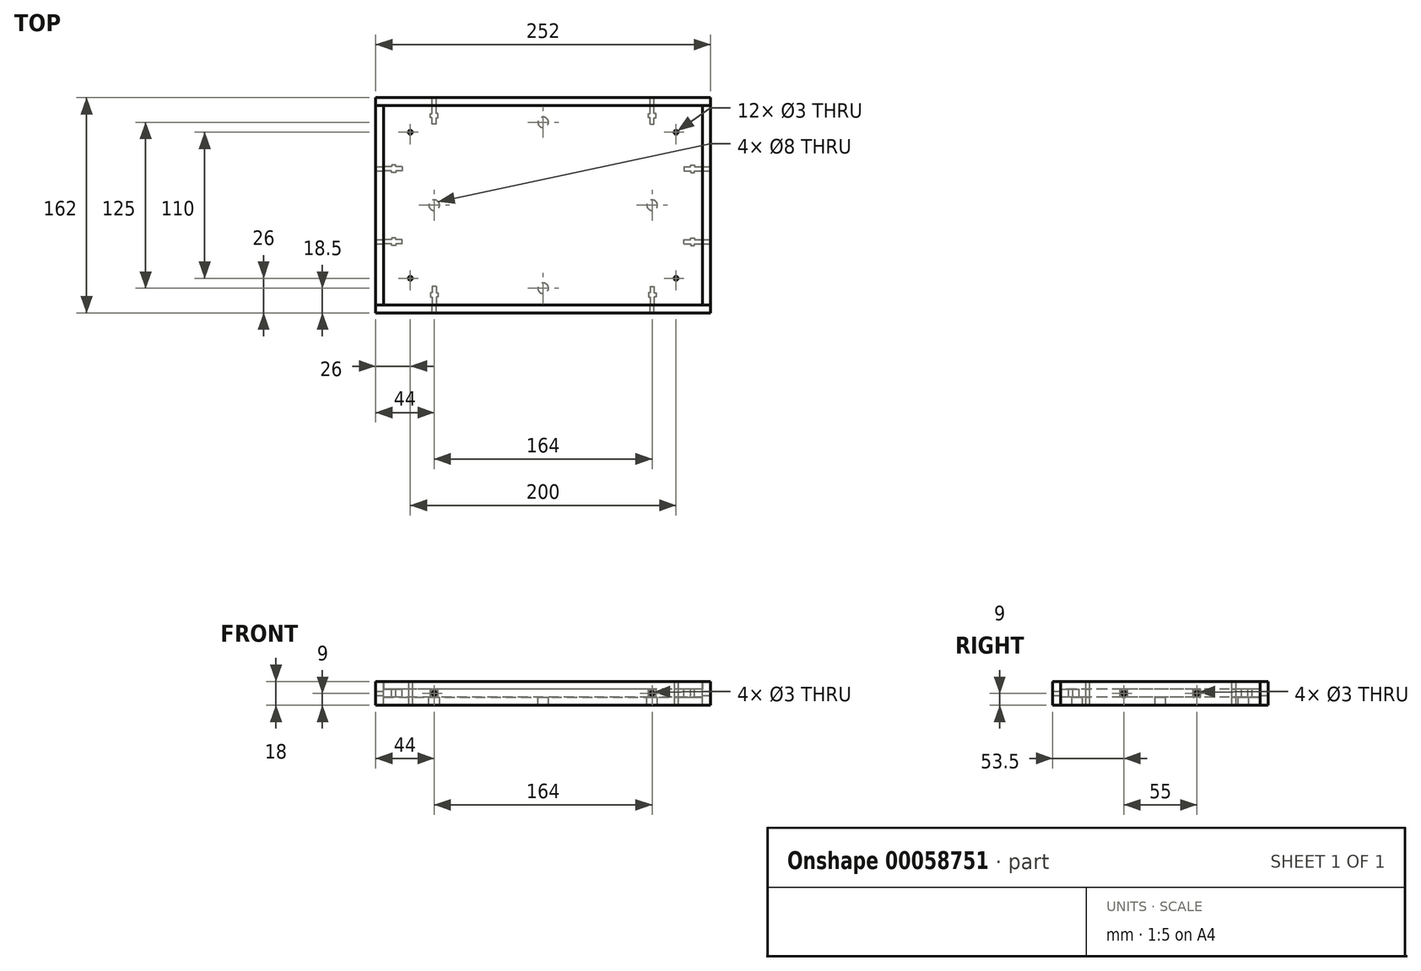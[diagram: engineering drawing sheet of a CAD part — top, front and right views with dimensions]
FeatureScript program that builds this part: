
annotation { "Feature Type Name" : "Feature", "Feature Type Description" : "" }
export const myFeature = defineFeature(function(context is Context, id is Id, definition is map)
    precondition{}
    {
        {
            var Q0;
            Q0=qCreatedBy(makeId("Top.planeOp"),FACE);
            var sketch = newSketch(context, id + "F25", { "sketchPlane" : qUnion([Q0])});
            skLineSegment(sketch, "E0.rect.bottom", {"start": v(120, 75) * mm, "end": v(-120, 75) * mm});
            skLineSegment(sketch, "E0.rect.top", {"start": v(120, -75) * mm, "end": v(-120, -75) * mm});
            skLineSegment(sketch, "E0.rect.left", {"start": v(120, 75) * mm, "end": v(120, -75) * mm});
            skLineSegment(sketch, "E0.rect.right", {"start": v(-120, 75) * mm, "end": v(-120, -75) * mm});
            skPoint(sketch, "E0.rect.middle", {"position": v(0, 0) * mm});
            skSolve(sketch);
        }
        {
            var Q0;
            Q0=makeQuery(id+"F25.imprint","IMPRINT",FACE,{"disambiguationData":[TD([[makeQuery(id+"F25.imprint","IMPRINT",EDGE,{"derivedFrom":sQuery(id+"F25.wireOp",EDGE,"E0.rect.bottom")}),1.0]])]});
            extrude(context, id + "F0", {"entities" : qUnion([Q0]), "depth" : 6 * mm});
        }
        {
            var Q0;
            Q0=makeQuery(id+"F0.opExtrude","CAP_FACE",FACE,{"disambiguationData":[OSD([sQuery(id+"F25.wireOp",EDGE,"E0.rect.bottom"),sQuery(id+"F25.wireOp",EDGE,"E0.rect.top"),sQuery(id+"F25.wireOp",EDGE,"E0.rect.left"),sQuery(id+"F25.wireOp",EDGE,"E0.rect.right")])],"isStart":true});
            extrude(context, id + "F1", {"entities" : qUnion([Q0]), "depth" : 6 * mm});
        }
        {
            var Q0;
            Q0=makeQuery(id+"F1.opExtrude","CAP_FACE",FACE,{"disambiguationData":[OSD([sQuery(id+"F25.wireOp",EDGE,"E0.rect.bottom"),sQuery(id+"F25.wireOp",EDGE,"E0.rect.top"),sQuery(id+"F25.wireOp",EDGE,"E0.rect.left"),sQuery(id+"F25.wireOp",EDGE,"E0.rect.right")])],"isStart":true});
            var sketch = newSketch(context, id + "F2", { "sketchPlane" : qUnion([Q0])});
            skLineSegment(sketch, "E1", {"start": v(106, -27.5) * mm, "end": v(120, -27.5) * mm, "construction": true});
            skLineSegment(sketch, "E2", {"start": v(120, -29) * mm, "end": v(114, -29) * mm});
            skLineSegment(sketch, "E3", {"start": v(114, -29) * mm, "end": v(114, -30.35) * mm});
            skLineSegment(sketch, "E4", {"start": v(114, -30.35) * mm, "end": v(111, -30.35) * mm});
            skLineSegment(sketch, "E5", {"start": v(111, -30.35) * mm, "end": v(111, -29) * mm});
            skLineSegment(sketch, "E6", {"start": v(111, -29) * mm, "end": v(106, -29) * mm});
            skLineSegment(sketch, "E7", {"start": v(106, -29) * mm, "end": v(106, -27.5) * mm});
            skLineSegment(sketch, "E8", {"start": v(120, -29) * mm, "end": v(120, -27.5) * mm});
            skLineSegment(sketch, "E9.MirrorCS", {"start": v(120, -26) * mm, "end": v(120, -27.5) * mm});
            skLineSegment(sketch, "E10.MirrorCS", {"start": v(120, -26) * mm, "end": v(114, -26) * mm});
            skLineSegment(sketch, "E11.MirrorCS", {"start": v(114, -26) * mm, "end": v(114, -24.65) * mm});
            skLineSegment(sketch, "E12.MirrorCS", {"start": v(114, -24.65) * mm, "end": v(111, -24.65) * mm});
            skLineSegment(sketch, "E13.MirrorCS", {"start": v(111, -24.65) * mm, "end": v(111, -26) * mm});
            skLineSegment(sketch, "E14.MirrorCS", {"start": v(111, -26) * mm, "end": v(106, -26) * mm});
            skLineSegment(sketch, "E15.MirrorCS", {"start": v(106, -26) * mm, "end": v(106, -27.5) * mm});
            skLineSegment(sketch, "E16", {"start": v(82, -61) * mm, "end": v(82, -75) * mm, "construction": true});
            skLineSegment(sketch, "E17", {"start": v(82, -75) * mm, "end": v(80.5, -75) * mm});
            skLineSegment(sketch, "E18", {"start": v(80.5, -75) * mm, "end": v(80.5, -69) * mm});
            skLineSegment(sketch, "E19", {"start": v(80.5, -69) * mm, "end": v(79.15, -69) * mm});
            skLineSegment(sketch, "E20", {"start": v(79.15, -69) * mm, "end": v(79.15, -66) * mm});
            skLineSegment(sketch, "E21", {"start": v(79.15, -66) * mm, "end": v(80.5, -66) * mm});
            skLineSegment(sketch, "E22", {"start": v(80.5, -66) * mm, "end": v(80.5, -61) * mm});
            skLineSegment(sketch, "E23", {"start": v(80.5, -61) * mm, "end": v(82, -61) * mm});
            skLineSegment(sketch, "E24.MirrorCS", {"start": v(82, -75) * mm, "end": v(83.5, -75) * mm});
            skLineSegment(sketch, "E25.MirrorCS", {"start": v(83.5, -75) * mm, "end": v(83.5, -69) * mm});
            skLineSegment(sketch, "E26.MirrorCS", {"start": v(83.5, -69) * mm, "end": v(84.85, -69) * mm});
            skLineSegment(sketch, "E27.MirrorCS", {"start": v(84.85, -69) * mm, "end": v(84.85, -66) * mm});
            skLineSegment(sketch, "E28.MirrorCS", {"start": v(84.85, -66) * mm, "end": v(83.5, -66) * mm});
            skLineSegment(sketch, "E29.MirrorCS", {"start": v(83.5, -66) * mm, "end": v(83.5, -61) * mm});
            skLineSegment(sketch, "E30.MirrorCS", {"start": v(83.5, -61) * mm, "end": v(82, -61) * mm});
            skSolve(sketch);
        }
        {
            var Q0;
            Q0=makeQuery(id+"F2.imprint","IMPRINT",FACE,{"disambiguationData":[TD([[makeQuery(id+"F2.imprint","IMPRINT",EDGE,{"derivedFrom":sQuery(id+"F2.wireOp",EDGE,"E17")}),-1.0]])]});
            var Q1;
            Q1=makeQuery(id+"F2.imprint","IMPRINT",FACE,{"disambiguationData":[TD([[makeQuery(id+"F2.imprint","IMPRINT",EDGE,{"derivedFrom":sQuery(id+"F2.wireOp",EDGE,"E2")}),-1.0]])]});
            var Q2;
            Q2=makeQuery(id+"F1.opExtrude","CAP_FACE",FACE,{"disambiguationData":[OSD([sQuery(id+"F25.wireOp",EDGE,"E0.rect.bottom"),sQuery(id+"F25.wireOp",EDGE,"E0.rect.top"),sQuery(id+"F25.wireOp",EDGE,"E0.rect.left"),sQuery(id+"F25.wireOp",EDGE,"E0.rect.right")])],"isStart":false});
            extrude(context, id + "F3", {"entities" : qUnion([Q0, Q1]), "endBound" : BoundingType.UP_TO_SURFACE, "oppositeDirection" : true, "endBoundEntityFace" : qUnion([Q2]), "depth" : 25 * mm});
        }
        {
            var Q0;
            Q0=makeQuery(id+"F3.opExtrude","SWEPT_BODY",BODY,{"disambiguationData":[OSD([sQuery(id+"F2.wireOp",EDGE,"E17"),sQuery(id+"F2.wireOp",EDGE,"E18"),sQuery(id+"F2.wireOp",EDGE,"E19"),sQuery(id+"F2.wireOp",EDGE,"E20"),sQuery(id+"F2.wireOp",EDGE,"E21"),sQuery(id+"F2.wireOp",EDGE,"E22"),sQuery(id+"F2.wireOp",EDGE,"E23"),sQuery(id+"F2.wireOp",EDGE,"E24.MirrorCS"),sQuery(id+"F2.wireOp",EDGE,"E25.MirrorCS"),sQuery(id+"F2.wireOp",EDGE,"E26.MirrorCS"),sQuery(id+"F2.wireOp",EDGE,"E27.MirrorCS"),sQuery(id+"F2.wireOp",EDGE,"E28.MirrorCS"),sQuery(id+"F2.wireOp",EDGE,"E29.MirrorCS"),sQuery(id+"F2.wireOp",EDGE,"E30.MirrorCS")])]});
            var Q1;
            Q1=makeQuery(id+"F3.opExtrude","SWEPT_BODY",BODY,{"disambiguationData":[OSD([sQuery(id+"F2.wireOp",EDGE,"E2"),sQuery(id+"F2.wireOp",EDGE,"E3"),sQuery(id+"F2.wireOp",EDGE,"E4"),sQuery(id+"F2.wireOp",EDGE,"E5"),sQuery(id+"F2.wireOp",EDGE,"E6"),sQuery(id+"F2.wireOp",EDGE,"E7"),sQuery(id+"F2.wireOp",EDGE,"E8"),sQuery(id+"F2.wireOp",EDGE,"E9.MirrorCS"),sQuery(id+"F2.wireOp",EDGE,"E10.MirrorCS"),sQuery(id+"F2.wireOp",EDGE,"E11.MirrorCS"),sQuery(id+"F2.wireOp",EDGE,"E12.MirrorCS"),sQuery(id+"F2.wireOp",EDGE,"E13.MirrorCS"),sQuery(id+"F2.wireOp",EDGE,"E14.MirrorCS"),sQuery(id+"F2.wireOp",EDGE,"E15.MirrorCS")])]});
            var Q2;
            Q2=qCreatedBy(makeId("Front.planeOp"),FACE);
            mirror(context, id + "F4", {"entities" : qUnion([Q0, Q1]), "mirrorPlane" : qUnion([Q2])});
        }
        {
            var Q0;
            Q0=makeQuery(id+"F3.opExtrude","SWEPT_BODY",BODY,{"disambiguationData":[OSD([sQuery(id+"F2.wireOp",EDGE,"E17"),sQuery(id+"F2.wireOp",EDGE,"E18"),sQuery(id+"F2.wireOp",EDGE,"E19"),sQuery(id+"F2.wireOp",EDGE,"E20"),sQuery(id+"F2.wireOp",EDGE,"E21"),sQuery(id+"F2.wireOp",EDGE,"E22"),sQuery(id+"F2.wireOp",EDGE,"E23"),sQuery(id+"F2.wireOp",EDGE,"E24.MirrorCS"),sQuery(id+"F2.wireOp",EDGE,"E25.MirrorCS"),sQuery(id+"F2.wireOp",EDGE,"E26.MirrorCS"),sQuery(id+"F2.wireOp",EDGE,"E27.MirrorCS"),sQuery(id+"F2.wireOp",EDGE,"E28.MirrorCS"),sQuery(id+"F2.wireOp",EDGE,"E29.MirrorCS"),sQuery(id+"F2.wireOp",EDGE,"E30.MirrorCS")])]});
            var Q1;
            Q1=makeQuery(id+"F3.opExtrude","SWEPT_BODY",BODY,{"disambiguationData":[OSD([sQuery(id+"F2.wireOp",EDGE,"E2"),sQuery(id+"F2.wireOp",EDGE,"E3"),sQuery(id+"F2.wireOp",EDGE,"E4"),sQuery(id+"F2.wireOp",EDGE,"E5"),sQuery(id+"F2.wireOp",EDGE,"E6"),sQuery(id+"F2.wireOp",EDGE,"E7"),sQuery(id+"F2.wireOp",EDGE,"E8"),sQuery(id+"F2.wireOp",EDGE,"E9.MirrorCS"),sQuery(id+"F2.wireOp",EDGE,"E10.MirrorCS"),sQuery(id+"F2.wireOp",EDGE,"E11.MirrorCS"),sQuery(id+"F2.wireOp",EDGE,"E12.MirrorCS"),sQuery(id+"F2.wireOp",EDGE,"E13.MirrorCS"),sQuery(id+"F2.wireOp",EDGE,"E14.MirrorCS"),sQuery(id+"F2.wireOp",EDGE,"E15.MirrorCS")])]});
            var Q2;
            Q2=makeQuery(id+"F4.opPattern","COPY",BODY,{"derivedFrom":makeQuery(id+"F3.opExtrude","SWEPT_BODY",BODY,{"disambiguationData":[OSD([sQuery(id+"F2.wireOp",EDGE,"E2"),sQuery(id+"F2.wireOp",EDGE,"E3"),sQuery(id+"F2.wireOp",EDGE,"E4"),sQuery(id+"F2.wireOp",EDGE,"E5"),sQuery(id+"F2.wireOp",EDGE,"E6"),sQuery(id+"F2.wireOp",EDGE,"E7"),sQuery(id+"F2.wireOp",EDGE,"E8"),sQuery(id+"F2.wireOp",EDGE,"E9.MirrorCS"),sQuery(id+"F2.wireOp",EDGE,"E10.MirrorCS"),sQuery(id+"F2.wireOp",EDGE,"E11.MirrorCS"),sQuery(id+"F2.wireOp",EDGE,"E12.MirrorCS"),sQuery(id+"F2.wireOp",EDGE,"E13.MirrorCS"),sQuery(id+"F2.wireOp",EDGE,"E14.MirrorCS"),sQuery(id+"F2.wireOp",EDGE,"E15.MirrorCS")])]}),"instanceName":"1"});
            var Q3;
            Q3=makeQuery(id+"F4.opPattern","COPY",BODY,{"derivedFrom":makeQuery(id+"F3.opExtrude","SWEPT_BODY",BODY,{"disambiguationData":[OSD([sQuery(id+"F2.wireOp",EDGE,"E17"),sQuery(id+"F2.wireOp",EDGE,"E18"),sQuery(id+"F2.wireOp",EDGE,"E19"),sQuery(id+"F2.wireOp",EDGE,"E20"),sQuery(id+"F2.wireOp",EDGE,"E21"),sQuery(id+"F2.wireOp",EDGE,"E22"),sQuery(id+"F2.wireOp",EDGE,"E23"),sQuery(id+"F2.wireOp",EDGE,"E24.MirrorCS"),sQuery(id+"F2.wireOp",EDGE,"E25.MirrorCS"),sQuery(id+"F2.wireOp",EDGE,"E26.MirrorCS"),sQuery(id+"F2.wireOp",EDGE,"E27.MirrorCS"),sQuery(id+"F2.wireOp",EDGE,"E28.MirrorCS"),sQuery(id+"F2.wireOp",EDGE,"E29.MirrorCS"),sQuery(id+"F2.wireOp",EDGE,"E30.MirrorCS")])]}),"instanceName":"1"});
            var Q4;
            Q4=qCreatedBy(makeId("Right.planeOp"),FACE);
            mirror(context, id + "F5", {"operationType" : NewBodyOperationType.REMOVE, "entities" : qUnion([Q0, Q1, Q2, Q3]), "mirrorPlane" : qUnion([Q4])});
        }
        {
            var Q0;
            Q0=makeQuery(id+"F3.opExtrude","SWEPT_BODY",BODY,{"disambiguationData":[OSD([sQuery(id+"F2.wireOp",EDGE,"E17"),sQuery(id+"F2.wireOp",EDGE,"E18"),sQuery(id+"F2.wireOp",EDGE,"E19"),sQuery(id+"F2.wireOp",EDGE,"E20"),sQuery(id+"F2.wireOp",EDGE,"E21"),sQuery(id+"F2.wireOp",EDGE,"E22"),sQuery(id+"F2.wireOp",EDGE,"E23"),sQuery(id+"F2.wireOp",EDGE,"E24.MirrorCS"),sQuery(id+"F2.wireOp",EDGE,"E25.MirrorCS"),sQuery(id+"F2.wireOp",EDGE,"E26.MirrorCS"),sQuery(id+"F2.wireOp",EDGE,"E27.MirrorCS"),sQuery(id+"F2.wireOp",EDGE,"E28.MirrorCS"),sQuery(id+"F2.wireOp",EDGE,"E29.MirrorCS"),sQuery(id+"F2.wireOp",EDGE,"E30.MirrorCS")])]});
            var Q1;
            Q1=makeQuery(id+"F3.opExtrude","SWEPT_BODY",BODY,{"disambiguationData":[OSD([sQuery(id+"F2.wireOp",EDGE,"E2"),sQuery(id+"F2.wireOp",EDGE,"E3"),sQuery(id+"F2.wireOp",EDGE,"E4"),sQuery(id+"F2.wireOp",EDGE,"E5"),sQuery(id+"F2.wireOp",EDGE,"E6"),sQuery(id+"F2.wireOp",EDGE,"E7"),sQuery(id+"F2.wireOp",EDGE,"E8"),sQuery(id+"F2.wireOp",EDGE,"E9.MirrorCS"),sQuery(id+"F2.wireOp",EDGE,"E10.MirrorCS"),sQuery(id+"F2.wireOp",EDGE,"E11.MirrorCS"),sQuery(id+"F2.wireOp",EDGE,"E12.MirrorCS"),sQuery(id+"F2.wireOp",EDGE,"E13.MirrorCS"),sQuery(id+"F2.wireOp",EDGE,"E14.MirrorCS"),sQuery(id+"F2.wireOp",EDGE,"E15.MirrorCS")])]});
            var Q2;
            Q2=makeQuery(id+"F4.opPattern","COPY",BODY,{"derivedFrom":makeQuery(id+"F3.opExtrude","SWEPT_BODY",BODY,{"disambiguationData":[OSD([sQuery(id+"F2.wireOp",EDGE,"E2"),sQuery(id+"F2.wireOp",EDGE,"E3"),sQuery(id+"F2.wireOp",EDGE,"E4"),sQuery(id+"F2.wireOp",EDGE,"E5"),sQuery(id+"F2.wireOp",EDGE,"E6"),sQuery(id+"F2.wireOp",EDGE,"E7"),sQuery(id+"F2.wireOp",EDGE,"E8"),sQuery(id+"F2.wireOp",EDGE,"E9.MirrorCS"),sQuery(id+"F2.wireOp",EDGE,"E10.MirrorCS"),sQuery(id+"F2.wireOp",EDGE,"E11.MirrorCS"),sQuery(id+"F2.wireOp",EDGE,"E12.MirrorCS"),sQuery(id+"F2.wireOp",EDGE,"E13.MirrorCS"),sQuery(id+"F2.wireOp",EDGE,"E14.MirrorCS"),sQuery(id+"F2.wireOp",EDGE,"E15.MirrorCS")])]}),"instanceName":"1"});
            var Q3;
            Q3=makeQuery(id+"F4.opPattern","COPY",BODY,{"derivedFrom":makeQuery(id+"F3.opExtrude","SWEPT_BODY",BODY,{"disambiguationData":[OSD([sQuery(id+"F2.wireOp",EDGE,"E17"),sQuery(id+"F2.wireOp",EDGE,"E18"),sQuery(id+"F2.wireOp",EDGE,"E19"),sQuery(id+"F2.wireOp",EDGE,"E20"),sQuery(id+"F2.wireOp",EDGE,"E21"),sQuery(id+"F2.wireOp",EDGE,"E22"),sQuery(id+"F2.wireOp",EDGE,"E23"),sQuery(id+"F2.wireOp",EDGE,"E24.MirrorCS"),sQuery(id+"F2.wireOp",EDGE,"E25.MirrorCS"),sQuery(id+"F2.wireOp",EDGE,"E26.MirrorCS"),sQuery(id+"F2.wireOp",EDGE,"E27.MirrorCS"),sQuery(id+"F2.wireOp",EDGE,"E28.MirrorCS"),sQuery(id+"F2.wireOp",EDGE,"E29.MirrorCS"),sQuery(id+"F2.wireOp",EDGE,"E30.MirrorCS")])]}),"instanceName":"1"});
            var Q4;
            Q4=makeQuery(id+"F1.opExtrude","SWEPT_BODY",BODY,{"disambiguationData":[OSD([sQuery(id+"F25.wireOp",EDGE,"E0.rect.bottom"),sQuery(id+"F25.wireOp",EDGE,"E0.rect.top"),sQuery(id+"F25.wireOp",EDGE,"E0.rect.left"),sQuery(id+"F25.wireOp",EDGE,"E0.rect.right")])]});
            booleanBodies(context, id + "F6", {"operationType" : BooleanOperationType.SUBTRACTION, "tools" : qUnion([Q0, Q1, Q2, Q3]), "targets" : qUnion([Q4])});
        }
        {
            var Q0;
            Q0=makeQuery(id+"F1.opExtrude","CAP_FACE",FACE,{"disambiguationData":[OSD([sQuery(id+"F25.wireOp",EDGE,"E0.rect.bottom"),sQuery(id+"F25.wireOp",EDGE,"E0.rect.top"),sQuery(id+"F25.wireOp",EDGE,"E0.rect.left"),sQuery(id+"F25.wireOp",EDGE,"E0.rect.right")])],"isStart":false});
            var sketch = newSketch(context, id + "F7", { "sketchPlane" : qUnion([Q0])});
            skLineSegment(sketch, "E31", {"start": v(120, -75) * mm, "end": v(120, 75) * mm});
            skLineSegment(sketch, "E32", {"start": v(120, 75) * mm, "end": v(-120, 75) * mm});
            skLineSegment(sketch, "E33", {"start": v(-120, 75) * mm, "end": v(-120, -75) * mm});
            skLineSegment(sketch, "E34", {"start": v(-120, -75) * mm, "end": v(120, -75) * mm});
            skSolve(sketch);
        }
        {
            var Q0;
            Q0=qSketchRegion(id+"F7",true);
            extrude(context, id + "F8", {"entities" : qUnion([Q0]), "depth" : 6 * mm});
        }
        {
            var Q0;
            Q0=makeQuery(id+"F0.opExtrude","CAP_FACE",FACE,{"disambiguationData":[OSD([sQuery(id+"F25.wireOp",EDGE,"E0.rect.bottom"),sQuery(id+"F25.wireOp",EDGE,"E0.rect.top"),sQuery(id+"F25.wireOp",EDGE,"E0.rect.left"),sQuery(id+"F25.wireOp",EDGE,"E0.rect.right")])],"isStart":false});
            var sketch = newSketch(context, id + "F9", { "sketchPlane" : qUnion([Q0])});
            skPoint(sketch, "E35", {"position": v(82, 0) * mm});
            skPoint(sketch, "E36", {"position": v(0, -62.5) * mm});
            skPoint(sketch, "E37.MirrorP", {"position": v(0, 62.5) * mm});
            skPoint(sketch, "E38.MirrorP", {"position": v(-82, 0) * mm});
            skLineSegment(sketch, "E39", {"start": v(0, -62.5) * mm, "end": v(0, -75) * mm, "construction": true});
            skLineSegment(sketch, "E40", {"start": v(120, 0) * mm, "end": v(82, 0) * mm, "construction": true});
            skSolve(sketch);
        }
        {
            var Q0;
            Q0=sQuery(id+"F9.wireOp",VERTEX,"E35");
            var Q1;
            Q1=sQuery(id+"F9.wireOp",VERTEX,"E36");
            var Q2;
            Q2=sQuery(id+"F9.wireOp",VERTEX,"E37.MirrorP");
            var Q3;
            Q3=sQuery(id+"F9.wireOp",VERTEX,"E38.MirrorP");
            var Q4;
            Q4=makeQuery(id+"F8.opExtrude","SWEPT_BODY",BODY,{"disambiguationData":[OSD([sQuery(id+"F7.wireOp",EDGE,"E31"),sQuery(id+"F7.wireOp",EDGE,"E32"),sQuery(id+"F7.wireOp",EDGE,"E33"),sQuery(id+"F7.wireOp",EDGE,"E34")])]});
            hole(context, id + "F10", {"style" : HoleStyle.SIMPLE, "holeDiameter" : 8 * mm, "endStyle" : HoleEndStyle.THROUGH, "locations" : qUnion([Q0, Q1, Q2, Q3]), "scope" : qUnion([Q4])});
        }
        {
            var Q0;
            Q0=makeQuery(id+"F0.opExtrude","SWEPT_FACE",FACE,{"disambiguationData":[OSD([sQuery(id+"F25.wireOp",EDGE,"E0.rect.bottom")])]});
            var sketch = newSketch(context, id + "F11", { "sketchPlane" : qUnion([Q0])});
            skLineSegment(sketch, "E41", {"start": v(-126, 6) * mm, "end": v(-126, -12) * mm});
            skLineSegment(sketch, "E42", {"start": v(-126, -12) * mm, "end": v(126, -12) * mm});
            skLineSegment(sketch, "E43", {"start": v(126, -12) * mm, "end": v(126, 6) * mm});
            skLineSegment(sketch, "E44", {"start": v(126, 6) * mm, "end": v(-126, 6) * mm});
            skSolve(sketch);
        }
        {
            var Q0;
            Q0=qSketchRegion(id+"F11",true);
            extrude(context, id + "F12", {"entities" : qUnion([Q0]), "depth" : 6 * mm});
        }
        {
            var Q0;
            Q0=makeQuery(id+"F12.opExtrude","CAP_FACE",FACE,{"disambiguationData":[OSD([sQuery(id+"F11.wireOp",EDGE,"E41"),sQuery(id+"F11.wireOp",EDGE,"E42"),sQuery(id+"F11.wireOp",EDGE,"E43"),sQuery(id+"F11.wireOp",EDGE,"E44")])],"isStart":false});
            var sketch = newSketch(context, id + "F13", { "sketchPlane" : qUnion([Q0])});
            skLineSegment(sketch, "E45.0", {"start": v(-83.5, -6) * mm, "end": v(-83.5, 0) * mm, "construction": true});
            skLineSegment(sketch, "E46.0", {"start": v(-80.5, -6) * mm, "end": v(-80.5, 0) * mm, "construction": true});
            skLineSegment(sketch, "E47.0", {"start": v(80.5, -6) * mm, "end": v(80.5, 0) * mm, "construction": true});
            skLineSegment(sketch, "E48.0", {"start": v(83.5, -6) * mm, "end": v(83.5, 0) * mm, "construction": true});
            skLineSegment(sketch, "E49", {"start": v(-83.5, -3) * mm, "end": v(-80.5, -3) * mm, "construction": true});
            skLineSegment(sketch, "E50", {"start": v(80.5, -3) * mm, "end": v(83.5, -3) * mm, "construction": true});
            skPoint(sketch, "E51", {"position": v(-82, -3) * mm});
            skPoint(sketch, "E52", {"position": v(82, -3) * mm});
            skSolve(sketch);
        }
        {
            var Q0;
            Q0=sQuery(id+"F13.wireOp",VERTEX,"E51");
            var Q1;
            Q1=sQuery(id+"F13.wireOp",VERTEX,"E52");
            var Q2;
            Q2=makeQuery(id+"F12.opExtrude","SWEPT_BODY",BODY,{"disambiguationData":[OSD([sQuery(id+"F11.wireOp",EDGE,"E41"),sQuery(id+"F11.wireOp",EDGE,"E42"),sQuery(id+"F11.wireOp",EDGE,"E43"),sQuery(id+"F11.wireOp",EDGE,"E44")])]});
            hole(context, id + "F14", {"style" : HoleStyle.SIMPLE, "holeDiameter" : 3 * mm, "endStyle" : HoleEndStyle.THROUGH, "locations" : qUnion([Q0, Q1]), "scope" : qUnion([Q2])});
        }
        {
            var Q0;
            Q0=makeQuery(id+"F12.opExtrude","CAP_FACE",FACE,{"disambiguationData":[OSD([sQuery(id+"F11.wireOp",EDGE,"E41"),sQuery(id+"F11.wireOp",EDGE,"E42"),sQuery(id+"F11.wireOp",EDGE,"E43"),sQuery(id+"F11.wireOp",EDGE,"E44")])],"isStart":false});
            var sketch = newSketch(context, id + "F15", { "sketchPlane" : qUnion([Q0])});
            skPoint(sketch, "E53.0", {"position": v(-120, 6) * mm});
            skSolve(sketch);
        }
        {
            var Q0;
            Q0=makeQuery(id+"F12.opExtrude","SWEPT_BODY",BODY,{"disambiguationData":[OSD([sQuery(id+"F11.wireOp",EDGE,"E41"),sQuery(id+"F11.wireOp",EDGE,"E42"),sQuery(id+"F11.wireOp",EDGE,"E43"),sQuery(id+"F11.wireOp",EDGE,"E44")])]});
            var Q1;
            Q1=sQuery(id+"F15.wireOp",VERTEX,"E53.0");
            var Q2;
            Q2=makeQuery(id+"F0.opExtrude","CAP_VERTEX",VERTEX,{"disambiguationData":[OSD([sQuery(id+"F25.wireOp",EDGE,"E0.rect.top"),sQuery(id+"F25.wireOp",EDGE,"E0.rect.left")])],"isStart":false});
            transform(context, id + "F16", {"entities" : qUnion([Q0]), "transformType" : TransformType.TRANSLATION_ENTITY, "oppositeDirectionEntity" : false, "transformLine" : qUnion([Q1, Q2]), "makeCopy" : true});
        }
        {
            var Q0;
            Q0=makeQuery(id+"F0.opExtrude","SWEPT_FACE",FACE,{"disambiguationData":[OSD([sQuery(id+"F25.wireOp",EDGE,"E0.rect.left")])]});
            var sketch = newSketch(context, id + "F17", { "sketchPlane" : qUnion([Q0])});
            skLineSegment(sketch, "E54", {"start": v(-75, 6) * mm, "end": v(-75, -12) * mm});
            skLineSegment(sketch, "E55", {"start": v(-75, -12) * mm, "end": v(75, -12) * mm});
            skLineSegment(sketch, "E56", {"start": v(75, -12) * mm, "end": v(75, 6) * mm});
            skLineSegment(sketch, "E57", {"start": v(75, 6) * mm, "end": v(-75, 6) * mm});
            skSolve(sketch);
        }
        {
            var Q0;
            Q0=qSketchRegion(id+"F17",true);
            extrude(context, id + "F18", {"entities" : qUnion([Q0]), "depth" : 6 * mm});
        }
        {
            var Q0;
            Q0=makeQuery(id+"F18.opExtrude","CAP_FACE",FACE,{"disambiguationData":[OSD([sQuery(id+"F17.wireOp",EDGE,"E54"),sQuery(id+"F17.wireOp",EDGE,"E55"),sQuery(id+"F17.wireOp",EDGE,"E56"),sQuery(id+"F17.wireOp",EDGE,"E57")])],"isStart":false});
            var sketch = newSketch(context, id + "F19", { "sketchPlane" : qUnion([Q0])});
            skLineSegment(sketch, "E58.0", {"start": v(-29, -6) * mm, "end": v(-29, 0) * mm, "construction": true});
            skLineSegment(sketch, "E59.0", {"start": v(-26, -6) * mm, "end": v(-26, 0) * mm, "construction": true});
            skLineSegment(sketch, "E60.0", {"start": v(26, -6) * mm, "end": v(26, 0) * mm, "construction": true});
            skLineSegment(sketch, "E61.0", {"start": v(29, -6) * mm, "end": v(29, 0) * mm, "construction": true});
            skLineSegment(sketch, "E62", {"start": v(-29, -3) * mm, "end": v(-26, -3) * mm, "construction": true});
            skLineSegment(sketch, "E63", {"start": v(26, -3) * mm, "end": v(29, -3) * mm, "construction": true});
            skPoint(sketch, "E64", {"position": v(-27.5, -3) * mm});
            skPoint(sketch, "E65", {"position": v(27.5, -3) * mm});
            skSolve(sketch);
        }
        {
            var Q0;
            Q0=sQuery(id+"F19.wireOp",VERTEX,"E64");
            var Q1;
            Q1=sQuery(id+"F19.wireOp",VERTEX,"E65");
            var Q2;
            Q2=makeQuery(id+"F18.opExtrude","SWEPT_BODY",BODY,{"disambiguationData":[OSD([sQuery(id+"F17.wireOp",EDGE,"E54"),sQuery(id+"F17.wireOp",EDGE,"E55"),sQuery(id+"F17.wireOp",EDGE,"E56"),sQuery(id+"F17.wireOp",EDGE,"E57")])]});
            var Q3;
            Q3=makeQuery(id+"F18.opExtrude","SWEPT_BODY",BODY,{"disambiguationData":[OSD([sQuery(id+"F17.wireOp",EDGE,"E54"),sQuery(id+"F17.wireOp",EDGE,"E55"),sQuery(id+"F17.wireOp",EDGE,"E56"),sQuery(id+"F17.wireOp",EDGE,"E57")])]});
            hole(context, id + "F20", {"style" : HoleStyle.SIMPLE, "holeDiameter" : 3 * mm, "endStyle" : HoleEndStyle.THROUGH, "locations" : qUnion([Q0, Q1]), "scope" : qUnion([Q2, Q3])});
        }
        {
            var Q0;
            Q0=makeQuery(id+"F18.opExtrude","CAP_FACE",FACE,{"disambiguationData":[OSD([sQuery(id+"F17.wireOp",EDGE,"E54"),sQuery(id+"F17.wireOp",EDGE,"E55"),sQuery(id+"F17.wireOp",EDGE,"E56"),sQuery(id+"F17.wireOp",EDGE,"E57")])],"isStart":false});
            var sketch = newSketch(context, id + "F21", { "sketchPlane" : qUnion([Q0])});
            skPoint(sketch, "E66", {"position": v(-75, 6) * mm});
            skSolve(sketch);
        }
        {
            var Q0;
            Q0=makeQuery(id+"F18.opExtrude","SWEPT_BODY",BODY,{"disambiguationData":[OSD([sQuery(id+"F17.wireOp",EDGE,"E54"),sQuery(id+"F17.wireOp",EDGE,"E55"),sQuery(id+"F17.wireOp",EDGE,"E56"),sQuery(id+"F17.wireOp",EDGE,"E57")])]});
            var Q1;
            Q1=sQuery(id+"F21.wireOp",VERTEX,"E66");
            var Q2;
            Q2=makeQuery(id+"F0.opExtrude","CAP_VERTEX",VERTEX,{"disambiguationData":[OSD([sQuery(id+"F25.wireOp",EDGE,"E0.rect.top"),sQuery(id+"F25.wireOp",EDGE,"E0.rect.right")])],"isStart":false});
            transform(context, id + "F22", {"entities" : qUnion([Q0]), "transformType" : TransformType.TRANSLATION_ENTITY, "oppositeDirectionEntity" : false, "transformLine" : qUnion([Q1, Q2]), "makeCopy" : true});
        }
        {
            var Q0;
            Q0=makeQuery(id+"F8.opExtrude","CAP_FACE",FACE,{"disambiguationData":[OSD([sQuery(id+"F7.wireOp",EDGE,"E31"),sQuery(id+"F7.wireOp",EDGE,"E32"),sQuery(id+"F7.wireOp",EDGE,"E33"),sQuery(id+"F7.wireOp",EDGE,"E34")])],"isStart":false});
            var sketch = newSketch(context, id + "F23", { "sketchPlane" : qUnion([Q0])});
            skLineSegment(sketch, "E67.rect.bottom", {"start": v(100, 55) * mm, "end": v(-100, 55) * mm, "construction": true});
            skLineSegment(sketch, "E67.rect.top", {"start": v(100, -55) * mm, "end": v(-100, -55) * mm, "construction": true});
            skLineSegment(sketch, "E67.rect.left", {"start": v(100, 55) * mm, "end": v(100, -55) * mm, "construction": true});
            skLineSegment(sketch, "E67.rect.right", {"start": v(-100, 55) * mm, "end": v(-100, -55) * mm, "construction": true});
            skPoint(sketch, "E67.rect.middle", {"position": v(0, 0) * mm});
            skSolve(sketch);
        }
        {
            var Q0;
            Q0=sQuery(id+"F23.wireOp",VERTEX,"E67.rect.right.start");
            var Q1;
            Q1=sQuery(id+"F23.wireOp",VERTEX,"E67.rect.right.end");
            var Q2;
            Q2=sQuery(id+"F23.wireOp",VERTEX,"E67.rect.left.end");
            var Q3;
            Q3=sQuery(id+"F23.wireOp",VERTEX,"E67.rect.bottom.start");
            var Q4;
            Q4=makeQuery(id+"F8.opExtrude","SWEPT_BODY",BODY,{"disambiguationData":[OSD([sQuery(id+"F7.wireOp",EDGE,"E31"),sQuery(id+"F7.wireOp",EDGE,"E32"),sQuery(id+"F7.wireOp",EDGE,"E33"),sQuery(id+"F7.wireOp",EDGE,"E34")])]});
            var Q5;
            Q5=makeQuery(id+"F8.opExtrude","SWEPT_BODY",BODY,{"disambiguationData":[OSD([sQuery(id+"F7.wireOp",EDGE,"E31"),sQuery(id+"F7.wireOp",EDGE,"E32"),sQuery(id+"F7.wireOp",EDGE,"E33"),sQuery(id+"F7.wireOp",EDGE,"E34")])]});
            var Q6;
            Q6=makeQuery(id+"F1.opExtrude","SWEPT_BODY",BODY,{"disambiguationData":[OSD([sQuery(id+"F25.wireOp",EDGE,"E0.rect.bottom"),sQuery(id+"F25.wireOp",EDGE,"E0.rect.top"),sQuery(id+"F25.wireOp",EDGE,"E0.rect.left"),sQuery(id+"F25.wireOp",EDGE,"E0.rect.right")])]});
            var Q7;
            Q7=makeQuery(id+"F0.opExtrude","SWEPT_BODY",BODY,{"disambiguationData":[OSD([sQuery(id+"F25.wireOp",EDGE,"E0.rect.bottom"),sQuery(id+"F25.wireOp",EDGE,"E0.rect.top"),sQuery(id+"F25.wireOp",EDGE,"E0.rect.left"),sQuery(id+"F25.wireOp",EDGE,"E0.rect.right")])]});
            hole(context, id + "F24", {"style" : HoleStyle.SIMPLE, "holeDiameter" : 3 * mm, "endStyle" : HoleEndStyle.THROUGH, "locations" : qUnion([Q0, Q1, Q2, Q3]), "scope" : qUnion([Q4, Q5, Q6, Q7])});
        }
    });
